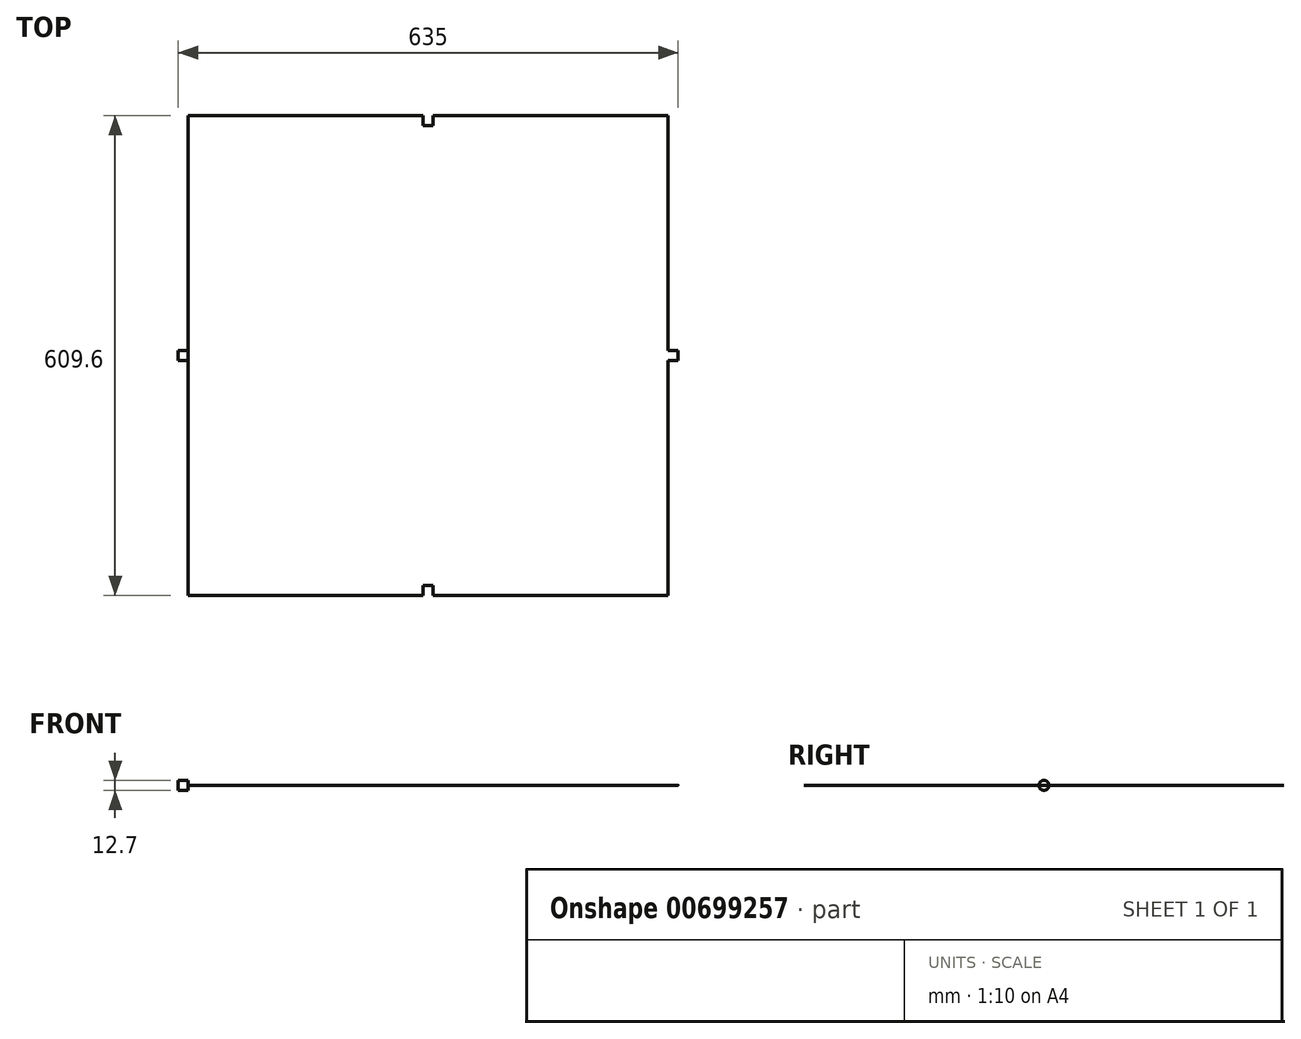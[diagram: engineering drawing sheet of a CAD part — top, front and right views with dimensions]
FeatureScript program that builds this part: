
annotation { "Feature Type Name" : "Feature", "Feature Type Description" : "" }
export const myFeature = defineFeature(function(context is Context, id is Id, definition is map)
    precondition{}
    {
        {
            var Q0;
            Q0=qCreatedBy(makeId("Top.planeOp"),FACE);
            var sketch = newSketch(context, id + "F0", { "sketchPlane" : qUnion([Q0])});
            skLineSegment(sketch, "E0.bottom", {"start": v(304.8, -304.8) * mm, "end": v(-304.8, -304.8) * mm});
            skLineSegment(sketch, "E0.top", {"start": v(304.8, 304.8) * mm, "end": v(-304.8, 304.8) * mm});
            skLineSegment(sketch, "E0.left", {"start": v(304.8, -304.8) * mm, "end": v(304.8, 304.8) * mm});
            skLineSegment(sketch, "E0.right", {"start": v(-304.8, -304.8) * mm, "end": v(-304.8, 304.8) * mm});
            skPoint(sketch, "E0.middle", {"position": v(0, 0) * mm});
            skSolve(sketch);
        }
        {
            var Q0;
            Q0=makeQuery(id+"F0.imprint","IMPRINT",FACE,{"disambiguationData":[TD([[makeQuery(id+"F0.imprint","IMPRINT",EDGE,{"derivedFrom":sQuery(id+"F0.wireOp",EDGE,"E0.bottom")}),-1.0]])]});
            extrude(context, id + "F1", {"entities" : qUnion([Q0]), "endBound" : BoundingType.SYMMETRIC, "oppositeDirection" : true, "depth" : 5 / 203.2 * mm, "offsetDistance" : 25.4 * mm});
        }
        {
            var Q0;
            Q0=makeQuery(id+"F1.opExtrude","SWEPT_FACE",FACE,{"disambiguationData":[OSD([sQuery(id+"F0.wireOp",EDGE,"E0.left")])]});
            var sketch = newSketch(context, id + "F2", { "sketchPlane" : qUnion([Q0])});
            skCircle(sketch, "E1", {"center": v(0, 0) * mm, "radius": 6.35 * mm});
            skSolve(sketch);
        }
        {
            var Q0;
            Q0=makeQuery(id+"F2.imprint","IMPRINT",FACE,{"disambiguationData":[TD([[makeQuery(id+"F2.imprint","IMPRINT",EDGE,{"derivedFrom":sQuery(id+"F2.wireOp",EDGE,"E1")}),1.0]])]});
            extrude(context, id + "F3", {"entities" : qUnion([Q0]), "operationType" : NewBodyOperationType.ADD, "depth" : 12.7 * mm, "offsetDistance" : 25.4 * mm});
        }
        {
            var Q0;
            Q0=makeQuery(id+"F1.opExtrude","SWEPT_FACE",FACE,{"disambiguationData":[OSD([sQuery(id+"F0.wireOp",EDGE,"E0.bottom")])]});
            var sketch = newSketch(context, id + "F4", { "sketchPlane" : qUnion([Q0])});
            skCircle(sketch, "E2", {"center": v(0, 0) * mm, "radius": 6.35 * mm});
            skSolve(sketch);
        }
        {
            var Q0;
            Q0=makeQuery(id+"F4.imprint","IMPRINT",FACE,{"disambiguationData":[TD([[makeQuery(id+"F4.imprint","IMPRINT",EDGE,{"derivedFrom":sQuery(id+"F4.wireOp",EDGE,"E2")}),1.0]])]});
            extrude(context, id + "F5", {"entities" : qUnion([Q0]), "operationType" : NewBodyOperationType.REMOVE, "oppositeDirection" : true, "depth" : 12.7 * mm, "offsetDistance" : 25.4 * mm});
        }
        {
            var Q0;
            Q0=makeQuery(id+"F1.opExtrude","SWEPT_FACE",FACE,{"disambiguationData":[OSD([sQuery(id+"F0.wireOp",EDGE,"E0.right")])]});
            var sketch = newSketch(context, id + "F6", { "sketchPlane" : qUnion([Q0])});
            skCircle(sketch, "E3", {"center": v(0, 0) * mm, "radius": 6.35 * mm});
            skSolve(sketch);
        }
        {
            var Q0;
            Q0 = qSketchRegion(id + "F6", true);
            extrude(context, id + "F7", {"entities" : qUnion([Q0]), "operationType" : NewBodyOperationType.ADD, "depth" : 12.7 * mm, "offsetDistance" : 25.4 * mm});
        }
        {
            var Q0;
            Q0=makeQuery(id+"F1.opExtrude","SWEPT_FACE",FACE,{"disambiguationData":[OSD([sQuery(id+"F0.wireOp",EDGE,"E0.top")])]});
            var sketch = newSketch(context, id + "F8", { "sketchPlane" : qUnion([Q0])});
            skCircle(sketch, "E4", {"center": v(0, 0) * mm, "radius": 6.35 * mm});
            skSolve(sketch);
        }
        {
            var Q0;
            Q0=makeQuery(id+"F8.imprint","IMPRINT",FACE,{"disambiguationData":[TD([[makeQuery(id+"F8.imprint","IMPRINT",EDGE,{"derivedFrom":sQuery(id+"F8.wireOp",EDGE,"E4")}),1.0]])]});
            extrude(context, id + "F9", {"entities" : qUnion([Q0]), "operationType" : NewBodyOperationType.REMOVE, "oppositeDirection" : true, "depth" : 12.7 * mm, "offsetDistance" : 25.4 * mm});
        }
    });
